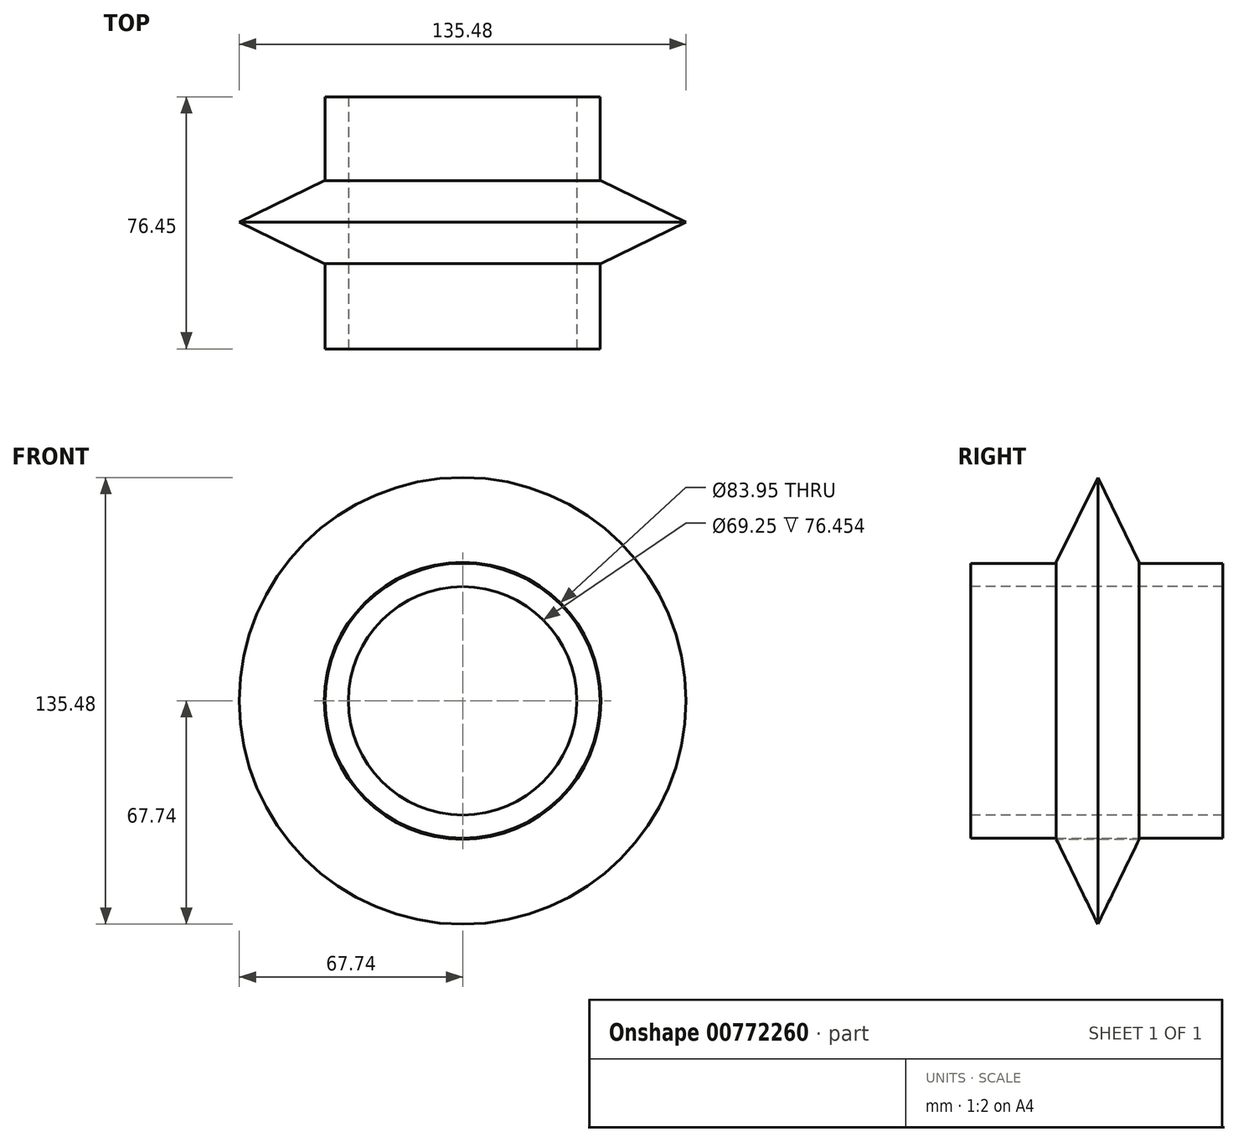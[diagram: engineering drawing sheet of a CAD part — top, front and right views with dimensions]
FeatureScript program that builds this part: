
annotation { "Feature Type Name" : "Feature", "Feature Type Description" : "" }
export const myFeature = defineFeature(function(context is Context, id is Id, definition is map)
    precondition{}
    {
        {
            var Q0;
            Q0=qCreatedBy(makeId("Front.planeOp"),FACE);
            var sketch = newSketch(context, id + "F0", { "sketchPlane" : qUnion([Q0])});
            skCircle(sketch, "E0", {"center": v(0, 0) * mm, "radius": 41.68 * mm});
            skSolve(sketch);
        }
        {
            var Q0;
            Q0 = qSketchRegion(id + "F0", true);
            extrude(context, id + "F1", {"entities" : qUnion([Q0]), "depth" : 25.65 * mm, "offsetDistance" : 25.4 * mm});
        }
        {
            var Q0;
            Q0=makeQuery(id+"F1.opExtrude","CAP_FACE",FACE,{"disambiguationData":[OSD([sQuery(id+"F0.wireOp",EDGE,"E0")])],"isStart":false});
            var sketch = newSketch(context, id + "F2", { "sketchPlane" : qUnion([Q0])});
            skCircle(sketch, "E1", {"center": v(0, 0) * mm, "radius": 34.62 * mm});
            skSolve(sketch);
        }
        {
            var Q0;
            Q0 = qSketchRegion(id + "F2", true);
            extrude(context, id + "F3", {"entities" : qUnion([Q0]), "operationType" : NewBodyOperationType.REMOVE, "oppositeDirection" : true, "depth" : 155.45 * mm, "offsetDistance" : 25.4 * mm});
        }
        {
            var Q0;
            Q0=qCreatedBy(makeId("Right.planeOp"),FACE);
            var sketch = newSketch(context, id + "F4", { "sketchPlane" : qUnion([Q0])});
            skLineSegment(sketch, "E2", {"start": v(0, 41.97) * mm, "end": v(-25.15, 41.97) * mm});
            skLineSegment(sketch, "E3", {"start": v(-25.15, 41.97) * mm, "end": v(-12.58, 67.74) * mm});
            skPoint(sketch, "E3.endSnap0", {"position": v(-12.58, 41.97) * mm});
            skLineSegment(sketch, "E4", {"start": v(-12.58, 67.74) * mm, "end": v(0, 41.97) * mm});
            skSolve(sketch);
        }
        {
            var Q0;
            Q0=makeQuery(id+"F4.imprint","IMPRINT",FACE,{"disambiguationData":[TD([[makeQuery(id+"F4.imprint","IMPRINT",EDGE,{"derivedFrom":sQuery(id+"F4.wireOp",EDGE,"E2")}),-1.0]])]});
            var Q1;
            Q1=makeQuery(id+"F1.opExtrude","SWEPT_FACE",FACE,{"disambiguationData":[OSD([sQuery(id+"F0.wireOp",EDGE,"E0")])]});
            revolve(context, id + "F5", {"surfaceOperationType" : NewSurfaceOperationType.NEW, "entities" : qUnion([Q0]), "axis" : qUnion([Q1]), "revolveType" : RevolveType.FULL});
        }
        {
            var Q0;
            Q0=makeQuery(id+"F1.opExtrude","CAP_FACE",FACE,{"disambiguationData":[OSD([sQuery(id+"F0.wireOp",EDGE,"E0")])],"isStart":false});
            extrude(context, id + "F6", {"entities" : qUnion([Q0]), "operationType" : NewBodyOperationType.ADD, "depth" : 25.4 * mm, "offsetDistance" : 25.4 * mm});
        }
        {
            var Q0;
            Q0=makeQuery(id+"F1.opExtrude","CAP_FACE",FACE,{"disambiguationData":[OSD([sQuery(id+"F0.wireOp",EDGE,"E0")])],"isStart":true});
            extrude(context, id + "F7", {"entities" : qUnion([Q0]), "operationType" : NewBodyOperationType.ADD, "depth" : 25.4 * mm, "offsetDistance" : 25.4 * mm});
        }
    });
